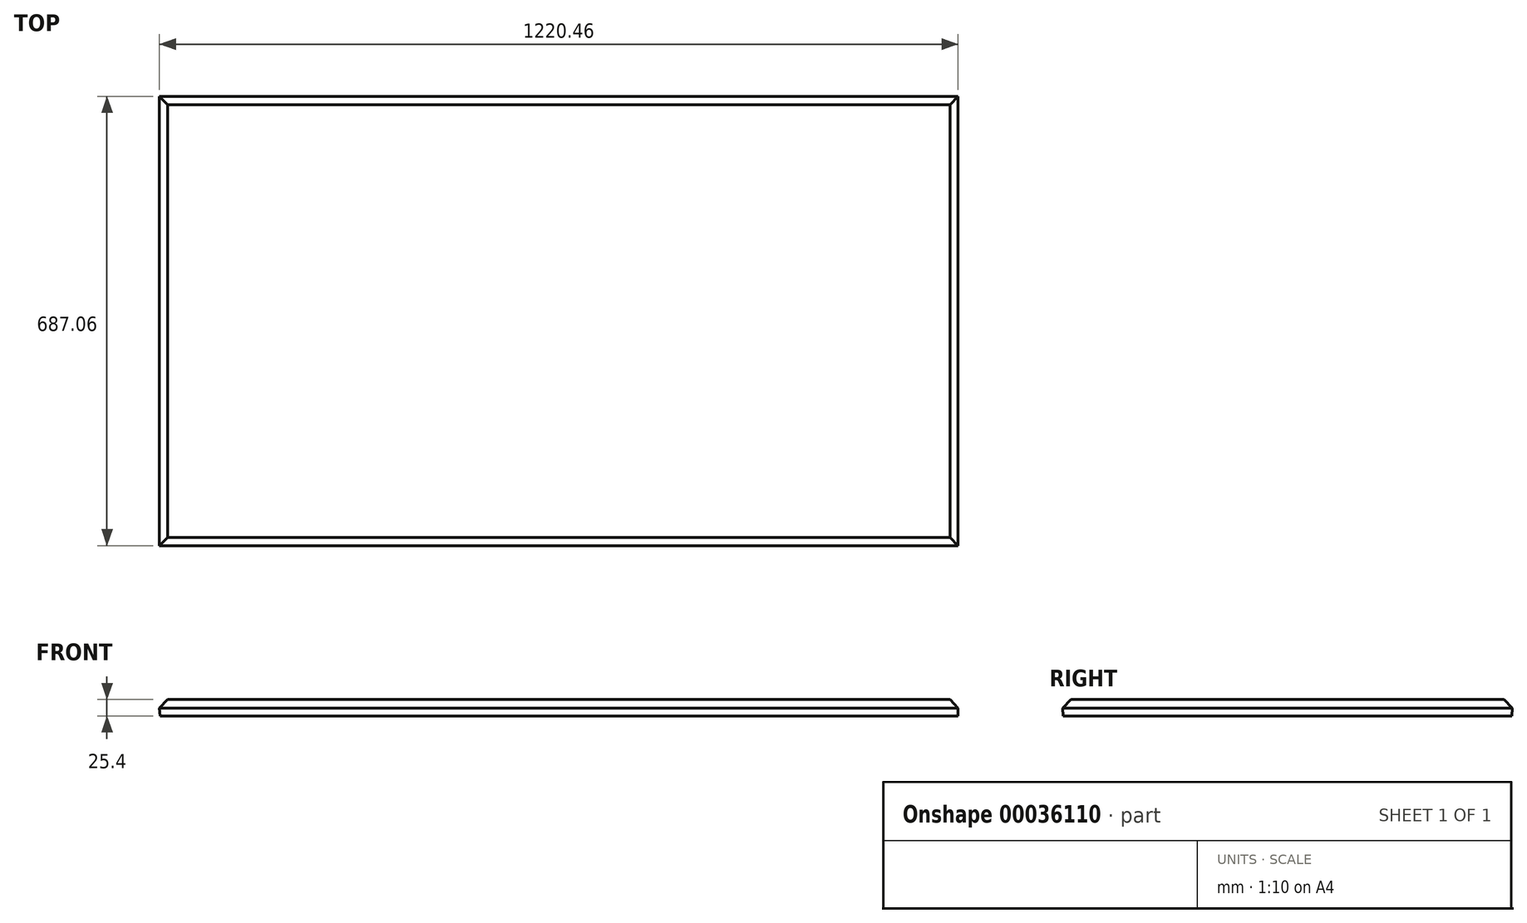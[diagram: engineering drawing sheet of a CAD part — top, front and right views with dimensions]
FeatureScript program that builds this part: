
annotation { "Feature Type Name" : "Feature", "Feature Type Description" : "" }
export const myFeature = defineFeature(function(context is Context, id is Id, definition is map)
    precondition{}
    {
        {
            var Q0;
            Q0=qCreatedBy(makeId("Top.planeOp"),FACE);
            var sketch = newSketch(context, id + "F0", { "sketchPlane" : qUnion([Q0])});
            skLineSegment(sketch, "E0.rect.bottom", {"start": v(609.6, 342.9) * mm, "end": v(-609.6, 342.9) * mm});
            skLineSegment(sketch, "E0.rect.top", {"start": v(609.6, -342.9) * mm, "end": v(-609.6, -342.9) * mm});
            skLineSegment(sketch, "E0.rect.left", {"start": v(609.6, 342.9) * mm, "end": v(609.6, -342.9) * mm});
            skLineSegment(sketch, "E0.rect.right", {"start": v(-609.6, 342.9) * mm, "end": v(-609.6, -342.9) * mm});
            skPoint(sketch, "E0.rect.middle", {"position": v(0, 0) * mm});
            skSolve(sketch);
        }
        {
            var Q0;
            Q0 = qSketchRegion(id + "F0", true);
            extrude(context, id + "F1", {"entities" : qUnion([Q0]), "depth" : 25.4 * mm, "hasDraft" : true, "draftAngle" : 3 * degree});
        }
        {
            var Q0;
            Q0=makeQuery(id+"F1.opExtrude","CAP_FACE",FACE,{"disambiguationData":[OSD([sQuery(id+"F0.wireOp",EDGE,"E0.rect.bottom"),sQuery(id+"F0.wireOp",EDGE,"E0.rect.top"),sQuery(id+"F0.wireOp",EDGE,"E0.rect.left"),sQuery(id+"F0.wireOp",EDGE,"E0.rect.right")])],"isStart":false});
            chamfer(context, id + "F2", {"entities" : qUnion([Q0]), "width" : 12.7 * mm, "tangentPropagation" : true});
        }
    });
